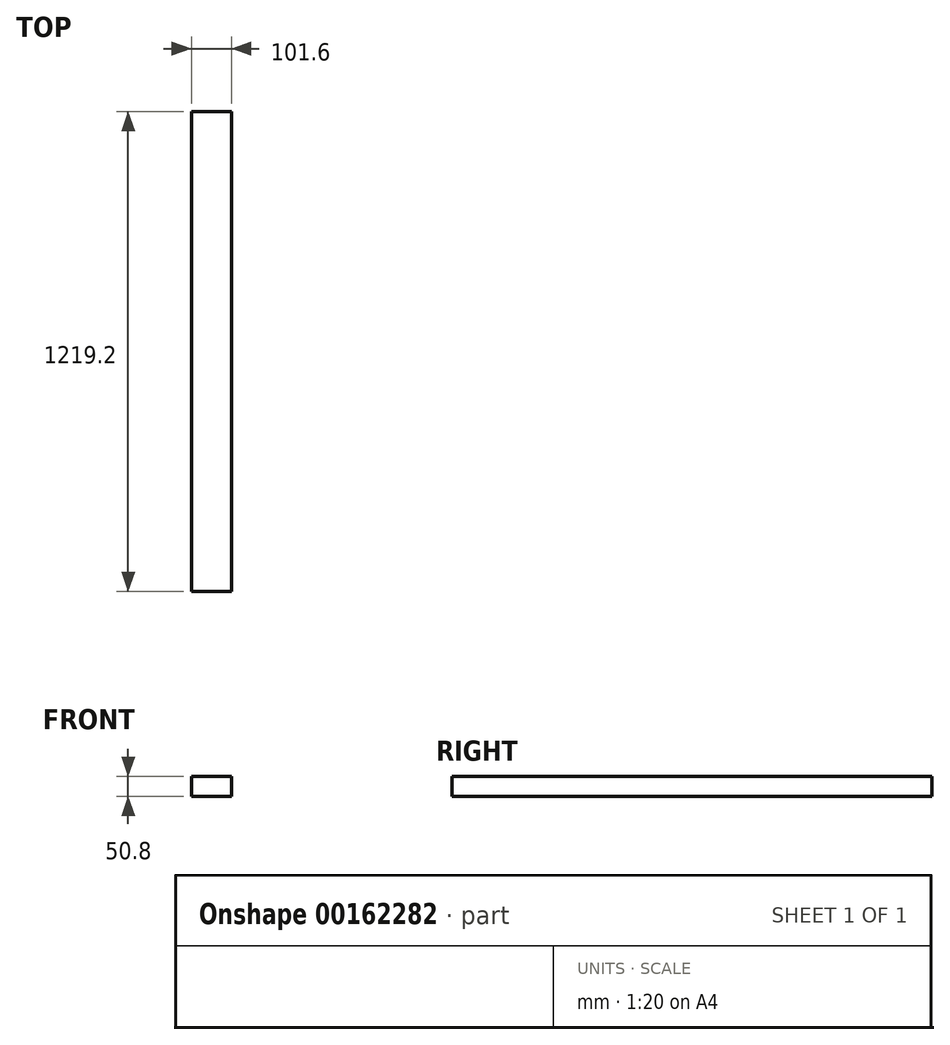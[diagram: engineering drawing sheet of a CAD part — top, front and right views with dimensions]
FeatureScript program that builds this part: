
annotation { "Feature Type Name" : "Feature", "Feature Type Description" : "" }
export const myFeature = defineFeature(function(context is Context, id is Id, definition is map)
    precondition{}
    {
        {
            var Q0;
            Q0=qCreatedBy(makeId("Top.planeOp"),FACE);
            var sketch = newSketch(context, id + "F0", { "sketchPlane" : qUnion([Q0])});
            skLineSegment(sketch, "E0.bottom", {"start": v(-203.57, -585.22) * mm, "end": v(-101.97, -585.22) * mm});
            skLineSegment(sketch, "E0.top", {"start": v(-203.57, 633.98) * mm, "end": v(-101.97, 633.98) * mm});
            skLineSegment(sketch, "E0.left", {"start": v(-203.57, -585.22) * mm, "end": v(-203.57, 633.98) * mm});
            skLineSegment(sketch, "E0.right", {"start": v(-101.97, -585.22) * mm, "end": v(-101.97, 633.98) * mm});
            skPoint(sketch, "E1", {"position": v(-101.97, -585.22) * mm});
            skPoint(sketch, "E2", {"position": v(-101.97, 24.38) * mm});
            skSolve(sketch);
        }
        {
            var Q0;
            Q0=makeQuery(id+"F0.imprint","IMPRINT",FACE,{"disambiguationData":[TD([[makeQuery(id+"F0.imprint","IMPRINT",EDGE,{"derivedFrom":sQuery(id+"F0.wireOp",EDGE,"E0.bottom")}),1.0]])]});
            extrude(context, id + "F1", {"entities" : qUnion([Q0]), "depth" : 50.8 * mm});
        }
    });
